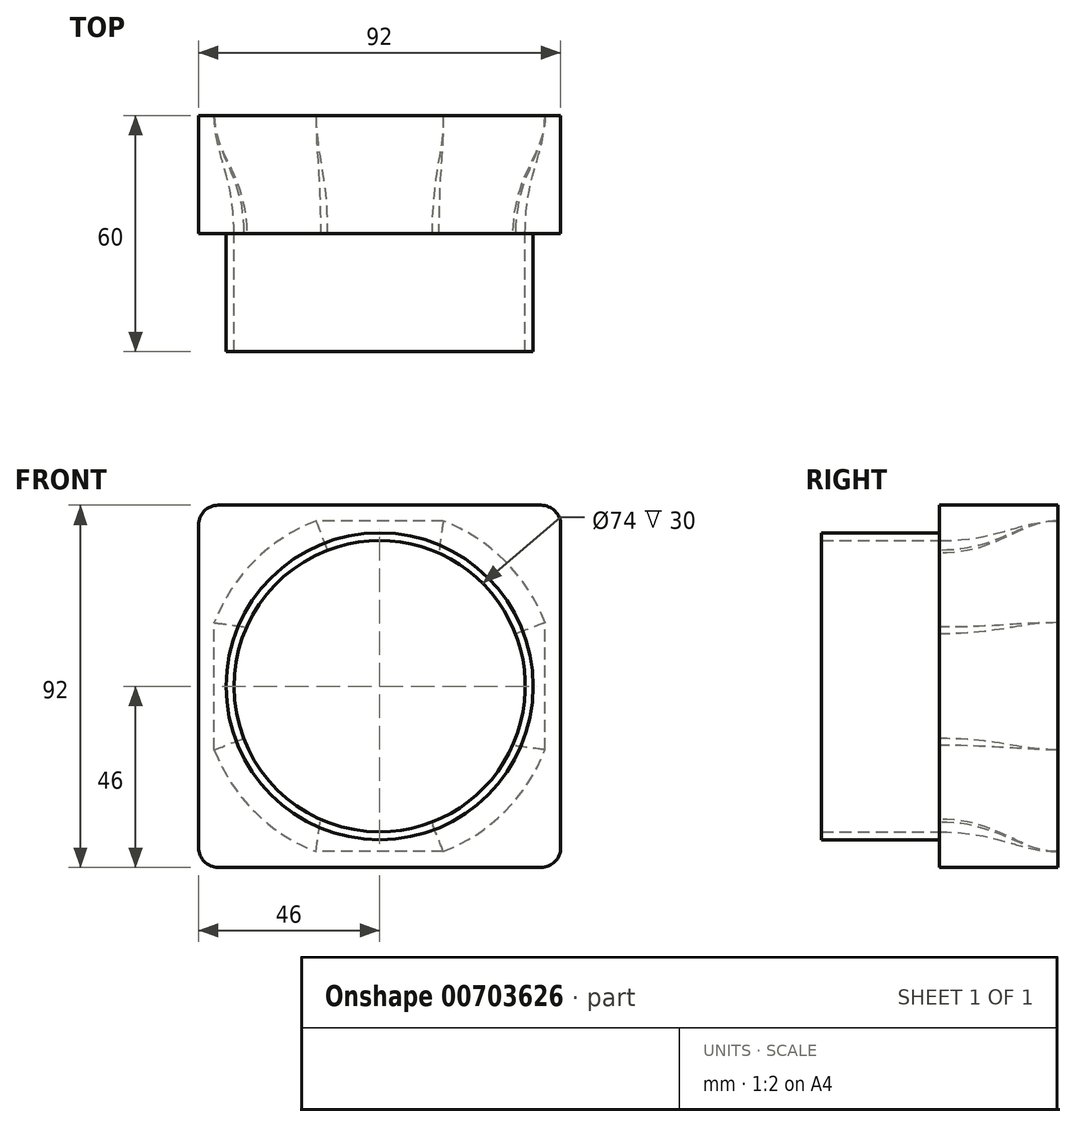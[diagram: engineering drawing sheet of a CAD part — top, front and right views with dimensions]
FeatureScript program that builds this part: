
annotation { "Feature Type Name" : "Feature", "Feature Type Description" : "" }
export const myFeature = defineFeature(function(context is Context, id is Id, definition is map)
    precondition{}
    {
        {
            var Q0;
            Q0=qCreatedBy(makeId("Front.planeOp"),FACE);
            var sketch = newSketch(context, id + "F0", { "sketchPlane" : qUnion([Q0])});
            skLineSegment(sketch, "E0.bottom", {"start": v(41, -46) * mm, "end": v(-41, -46) * mm});
            skLineSegment(sketch, "E0.top", {"start": v(41, 46) * mm, "end": v(-41, 46) * mm});
            skLineSegment(sketch, "E0.left", {"start": v(46, -41) * mm, "end": v(46, 41) * mm});
            skLineSegment(sketch, "E0.right", {"start": v(-46, -41) * mm, "end": v(-46, 41) * mm});
            skArc(sketch, "E1.filletArc", {"start": v(46, 41) * mm, "mid": v(44.54, 44.54) * mm, "end": v(41, 46) * mm});
            skArc(sketch, "E2.filletArc", {"start": v(41, -46) * mm, "mid": v(44.54, -44.54) * mm, "end": v(46, -41) * mm});
            skArc(sketch, "E3.filletArc", {"start": v(-46, -41) * mm, "mid": v(-44.54, -44.54) * mm, "end": v(-41, -46) * mm});
            skArc(sketch, "E4.filletArc", {"start": v(-41, 46) * mm, "mid": v(-44.54, 44.54) * mm, "end": v(-46, 41) * mm});
            skArc(sketch, "E5", {"start": v(-16.16, 42) * mm, "mid": v(-31.82, 31.82) * mm, "end": v(-42, 16.16) * mm});
            skArc(sketch, "E6.trimOffspring", {"start": v(-42, -16.16) * mm, "mid": v(-31.82, -31.82) * mm, "end": v(-16.16, -42) * mm});
            skArc(sketch, "E7.trimOffspring", {"start": v(16.16, -42) * mm, "mid": v(31.82, -31.82) * mm, "end": v(42, -16.16) * mm});
            skArc(sketch, "E8.trimOffspring", {"start": v(42, 16.16) * mm, "mid": v(31.82, 31.82) * mm, "end": v(16.16, 42) * mm});
            skLineSegment(sketch, "E9.0", {"start": v(16.16, 42) * mm, "end": v(-16.16, 42) * mm});
            skLineSegment(sketch, "E10.0", {"start": v(42, -16.16) * mm, "end": v(42, 16.16) * mm});
            skLineSegment(sketch, "E11.0", {"start": v(16.16, -42) * mm, "end": v(-16.16, -42) * mm});
            skLineSegment(sketch, "E12.0", {"start": v(-42, -16.16) * mm, "end": v(-42, 16.16) * mm});
            skSolve(sketch);
        }
        {
            var Q0;
            Q0=makeQuery(id+"F0.imprint","IMPRINT",FACE,{"disambiguationData":[TD([[makeQuery(id+"F0.imprint","IMPRINT",EDGE,{"derivedFrom":sQuery(id+"F0.wireOp",EDGE,"E0.bottom")}),-1.0]])]});
            var Q1;
            Q1=makeQuery(id+"F0.imprint","IMPRINT",FACE,{"disambiguationData":[TD([[makeQuery(id+"F0.imprint","IMPRINT",EDGE,{"derivedFrom":sQuery(id+"F0.wireOp",EDGE,"E5")}),1.0]])]});
            extrude(context, id + "F1", {"entities" : qUnion([Q0, Q1]), "depth" : 30 * mm, "offsetDistance" : 25 * mm});
        }
        {
            var Q0;
            Q0=qCreatedBy(makeId("Front.planeOp"),FACE);
            cPlane(context, id + "F2", {"entities" : qUnion([Q0]), "cplaneType" : CPlaneType.OFFSET, "offset" : 30 * mm, "width" : 150 * mm, "height" : 150 * mm});
        }
        {
            var Q0;
            Q0=qCreatedBy(id+"F2.planeOp",FACE);
            var sketch = newSketch(context, id + "F3", { "sketchPlane" : qUnion([Q0])});
            skCircle(sketch, "E13", {"center": v(0, 0) * mm, "radius": 37 * mm});
            skCircle(sketch, "E14", {"center": v(0, 0) * mm, "radius": 39 * mm});
            skSolve(sketch);
        }
        {
            var Q1;
            Q1=makeQuery(id+"F0.imprint","IMPRINT",FACE,{"disambiguationData":[TD([[makeQuery(id+"F0.imprint","IMPRINT",EDGE,{"derivedFrom":sQuery(id+"F0.wireOp",EDGE,"E5")}),1.0]])]});
            var Q2;
            Q2=makeQuery(id+"F3.imprint","IMPRINT",FACE,{"disambiguationData":[TD([[makeQuery(id+"F3.imprint","IMPRINT",EDGE,{"derivedFrom":sQuery(id+"F3.wireOp",EDGE,"E13")}),1.0]])]});
            loft(context, id + "F4", {"operationType" : NewBodyOperationType.REMOVE, "startCondition" : LoftEndDerivativeType.NORMAL_TO_PROFILE, "startMagnitude" : 1, "endCondition" : LoftEndDerivativeType.NORMAL_TO_PROFILE, "endMagnitude" : 1.5, "sheetProfilesArray" : [{ "sheetProfileEntities" : qUnion([Q1]) }, { "sheetProfileEntities" : qUnion([Q2]) }]});
        }
        {
            var Q0;
            Q0=makeQuery(id+"F3.imprint","IMPRINT",FACE,{"disambiguationData":[TD([[makeQuery(id+"F3.imprint","IMPRINT",EDGE,{"derivedFrom":sQuery(id+"F3.wireOp",EDGE,"E13")}),-1.0]])]});
            extrude(context, id + "F5", {"entities" : qUnion([Q0]), "operationType" : NewBodyOperationType.ADD, "depth" : 30 * mm, "offsetDistance" : 25 * mm});
        }
    });
